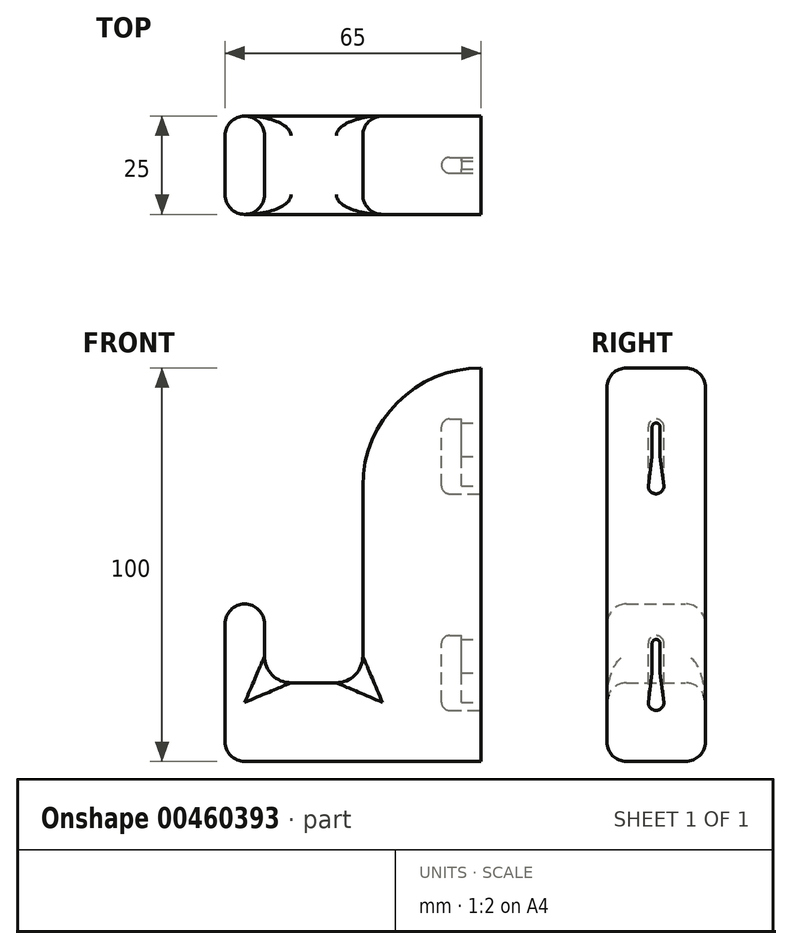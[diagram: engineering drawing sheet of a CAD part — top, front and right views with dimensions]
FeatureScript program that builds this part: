
annotation { "Feature Type Name" : "Feature", "Feature Type Description" : "" }
export const myFeature = defineFeature(function(context is Context, id is Id, definition is map)
    precondition{}
    {
        {
            var Q0;
            Q0=qCreatedBy(makeId("Front.planeOp"),FACE);
            var sketch = newSketch(context, id + "F0", { "sketchPlane" : qUnion([Q0])});
            skLineSegment(sketch, "E0", {"start": v(-32.5, 0) * mm, "end": v(32.5, 0) * mm});
            skLineSegment(sketch, "E1", {"start": v(32.5, 0) * mm, "end": v(32.5, 100) * mm});
            skLineSegment(sketch, "E2", {"start": v(32.5, 100) * mm, "end": v(2.5, 100) * mm});
            skLineSegment(sketch, "E3", {"start": v(2.5, 100) * mm, "end": v(2.5, 20) * mm});
            skLineSegment(sketch, "E4", {"start": v(2.5, 20) * mm, "end": v(-22.5, 20) * mm});
            skLineSegment(sketch, "E5", {"start": v(-22.5, 20) * mm, "end": v(-22.5, 40) * mm});
            skLineSegment(sketch, "E6", {"start": v(-22.5, 40) * mm, "end": v(-32.5, 40) * mm});
            skLineSegment(sketch, "E7", {"start": v(-32.5, 40) * mm, "end": v(-32.5, 0) * mm});
            skSolve(sketch);
        }
        {
            var Q0;
            Q0 = qSketchRegion(id + "F0", true);
            extrude(context, id + "F1", {"entities" : qUnion([Q0]), "endBound" : BoundingType.SYMMETRIC, "depth" : 25 * mm});
        }
        {
            var Q0;
            Q0=makeQuery(id+"F1.opExtrude","SWEPT_EDGE",EDGE,{"disambiguationData":[OSD([sQuery(id+"F0.wireOp",EDGE,"E6"),sQuery(id+"F0.wireOp",EDGE,"E7")])]});
            var Q1;
            Q1=makeQuery(id+"F1.opExtrude","SWEPT_EDGE",EDGE,{"disambiguationData":[OSD([sQuery(id+"F0.wireOp",EDGE,"E0"),sQuery(id+"F0.wireOp",EDGE,"E7")])]});
            var Q2;
            Q2=makeQuery(id+"F1.opExtrude","SWEPT_EDGE",EDGE,{"disambiguationData":[OSD([sQuery(id+"F0.wireOp",EDGE,"E5"),sQuery(id+"F0.wireOp",EDGE,"E6")])]});
            var Q3;
            Q3=makeQuery(id+"F1.opExtrude","CAP_EDGE",EDGE,{"disambiguationData":[OSD([sQuery(id+"F0.wireOp",EDGE,"E4")])],"isStart":false});
            var Q4;
            Q4=makeQuery(id+"F1.opExtrude","CAP_EDGE",EDGE,{"disambiguationData":[OSD([sQuery(id+"F0.wireOp",EDGE,"E4")])],"isStart":true});
            var Q5;
            Q5=makeQuery(id+"F1.opExtrude","CAP_EDGE",EDGE,{"disambiguationData":[OSD([sQuery(id+"F0.wireOp",EDGE,"E7")])],"isStart":false});
            var Q6;
            Q6=makeQuery(id+"F1.opExtrude","CAP_EDGE",EDGE,{"disambiguationData":[OSD([sQuery(id+"F0.wireOp",EDGE,"E5")])],"isStart":false});
            var Q7;
            Q7=makeQuery(id+"F1.opExtrude","CAP_EDGE",EDGE,{"disambiguationData":[OSD([sQuery(id+"F0.wireOp",EDGE,"E6")])],"isStart":false});
            var Q8;
            Q8=makeQuery(id+"F1.opExtrude","CAP_EDGE",EDGE,{"disambiguationData":[OSD([sQuery(id+"F0.wireOp",EDGE,"E6")])],"isStart":true});
            var Q9;
            Q9=makeQuery(id+"F1.opExtrude","CAP_EDGE",EDGE,{"disambiguationData":[OSD([sQuery(id+"F0.wireOp",EDGE,"E7")])],"isStart":true});
            var Q10;
            Q10=makeQuery(id+"F1.opExtrude","CAP_EDGE",EDGE,{"disambiguationData":[OSD([sQuery(id+"F0.wireOp",EDGE,"E5")])],"isStart":true});
            var Q11;
            Q11=makeQuery(id+"F1.opExtrude","CAP_EDGE",EDGE,{"disambiguationData":[OSD([sQuery(id+"F0.wireOp",EDGE,"E0")])],"isStart":false});
            var Q12;
            Q12=makeQuery(id+"F1.opExtrude","CAP_EDGE",EDGE,{"disambiguationData":[OSD([sQuery(id+"F0.wireOp",EDGE,"E0")])],"isStart":true});
            var Q13;
            Q13=makeQuery(id+"F1.opExtrude","CAP_EDGE",EDGE,{"disambiguationData":[OSD([sQuery(id+"F0.wireOp",EDGE,"E3")])],"isStart":false});
            var Q14;
            Q14=makeQuery(id+"F1.opExtrude","CAP_EDGE",EDGE,{"disambiguationData":[OSD([sQuery(id+"F0.wireOp",EDGE,"E3")])],"isStart":true});
            var Q15;
            Q15=makeQuery(id+"F1.opExtrude","CAP_EDGE",EDGE,{"disambiguationData":[OSD([sQuery(id+"F0.wireOp",EDGE,"E2")])],"isStart":false});
            var Q16;
            Q16=makeQuery(id+"F1.opExtrude","CAP_EDGE",EDGE,{"disambiguationData":[OSD([sQuery(id+"F0.wireOp",EDGE,"E2")])],"isStart":true});
            fillet(context, id + "F2", {"entities" : qUnion([Q0, Q1, Q2, Q3, Q4, Q5, Q6, Q7, Q8, Q9, Q10, Q11, Q12, Q13, Q14, Q15, Q16]), "radius" : 5 * mm, "tangentPropagation" : true, "allowEdgeOverflow" : false});
        }
        {
            var Q0;
            Q0=makeQuery(id+"F1.opExtrude","SWEPT_EDGE",EDGE,{"disambiguationData":[OSD([sQuery(id+"F0.wireOp",EDGE,"E2"),sQuery(id+"F0.wireOp",EDGE,"E3")])]});
            fillet(context, id + "F3", {"entities" : qUnion([Q0]), "radius" : 30 * mm, "tangentPropagation" : true, "allowEdgeOverflow" : false});
        }
        {
            var Q0;
            Q0=makeQuery(id+"F1.opExtrude","SWEPT_EDGE",EDGE,{"disambiguationData":[OSD([sQuery(id+"F0.wireOp",EDGE,"E3"),sQuery(id+"F0.wireOp",EDGE,"E4")])]});
            var Q1;
            Q1=makeQuery(id+"F1.opExtrude","SWEPT_EDGE",EDGE,{"disambiguationData":[OSD([sQuery(id+"F0.wireOp",EDGE,"E4"),sQuery(id+"F0.wireOp",EDGE,"E5")])]});
            fillet(context, id + "F4", {"entities" : qUnion([Q0, Q1]), "radius" : 6.75 * mm, "tangentPropagation" : true, "allowEdgeOverflow" : false});
        }
        {
            var Q0;
            Q0=makeQuery(id+"F1.opExtrude","SWEPT_FACE",FACE,{"disambiguationData":[OSD([sQuery(id+"F0.wireOp",EDGE,"E1")])]});
            var sketch = newSketch(context, id + "F5", { "sketchPlane" : qUnion([Q0])});
            skLineSegment(sketch, "E8", {"start": v(0, 15) * mm, "end": v(0, 30) * mm});
            skPoint(sketch, "E8.startSnap0", {"position": v(0, 0) * mm});
            skLineSegment(sketch, "E9", {"start": v(0, 70) * mm, "end": v(0, 85) * mm});
            skArc(sketch, "E10.0.startCap", {"start": v(2, 15) * mm, "mid": v(0, 13) * mm, "end": v(-2, 15) * mm});
            skArc(sketch, "E10.0.endCap", {"start": v(-2, 30) * mm, "mid": v(0, 32) * mm, "end": v(2, 30) * mm});
            skLineSegment(sketch, "E10.0.left", {"start": v(-2, 15) * mm, "end": v(-2, 30) * mm});
            skLineSegment(sketch, "E10.0.right", {"start": v(2, 15) * mm, "end": v(2, 30) * mm});
            skArc(sketch, "E10.1.startCap", {"start": v(2, 70) * mm, "mid": v(0, 68) * mm, "end": v(-2, 70) * mm});
            skArc(sketch, "E10.1.endCap", {"start": v(-2, 85) * mm, "mid": v(0, 87) * mm, "end": v(2, 85) * mm});
            skLineSegment(sketch, "E10.1.left", {"start": v(-2, 70) * mm, "end": v(-2, 85) * mm});
            skLineSegment(sketch, "E10.1.right", {"start": v(2, 70) * mm, "end": v(2, 85) * mm});
            skSolve(sketch);
        }
        {
            var Q0;
            Q0 = qSketchRegion(id + "F5", true);
            extrude(context, id + "F6", {"entities" : qUnion([Q0]), "operationType" : NewBodyOperationType.REMOVE, "oppositeDirection" : true, "depth" : 10 * mm});
        }
        {
            var Q0;
            Q0=makeQuery(id+"F1.opExtrude","SWEPT_FACE",FACE,{"disambiguationData":[OSD([sQuery(id+"F0.wireOp",EDGE,"E1")])]});
            var sketch = newSketch(context, id + "F7", { "sketchPlane" : qUnion([Q0])});
            skArc(sketch, "E11", {"start": v(1, 30) * mm, "mid": v(0, 31) * mm, "end": v(-1, 30) * mm});
            skLineSegment(sketch, "E12", {"start": v(2, 15) * mm, "end": v(2, 30) * mm});
            skArc(sketch, "E13", {"start": v(2, 30) * mm, "mid": v(0, 32) * mm, "end": v(-2, 30) * mm});
            skLineSegment(sketch, "E14", {"start": v(-2, 30) * mm, "end": v(-2, 15) * mm});
            skLineSegment(sketch, "E15", {"start": v(-2, 15) * mm, "end": v(-1, 22.5) * mm});
            skLineSegment(sketch, "E16", {"start": v(-1, 22.5) * mm, "end": v(-1, 30) * mm});
            skLineSegment(sketch, "E17", {"start": v(1, 30) * mm, "end": v(1, 22.5) * mm});
            skLineSegment(sketch, "E18", {"start": v(1, 22.5) * mm, "end": v(2, 15) * mm});
            skLineSegment(sketch, "E19.0.1.0", {"start": v(1, 77.5) * mm, "end": v(2, 70) * mm});
            skLineSegment(sketch, "E19.0.1.1", {"start": v(-1, 77.5) * mm, "end": v(-1, 85) * mm});
            skLineSegment(sketch, "E19.0.1.2", {"start": v(-2, 70) * mm, "end": v(-1, 77.5) * mm});
            skLineSegment(sketch, "E19.0.1.3", {"start": v(1, 85) * mm, "end": v(1, 77.5) * mm});
            skArc(sketch, "E19.0.1.4", {"start": v(1, 85) * mm, "mid": v(0, 86) * mm, "end": v(-1, 85) * mm});
            skLineSegment(sketch, "E19.0.1.5", {"start": v(2, 70) * mm, "end": v(2, 85) * mm});
            skLineSegment(sketch, "E19.0.1.6", {"start": v(-2, 85) * mm, "end": v(-2, 70) * mm});
            skArc(sketch, "E19.0.1.7", {"start": v(2, 85) * mm, "mid": v(0, 87) * mm, "end": v(-2, 85) * mm});
            skLineSegment(sketch, "E19.direction1", {"start": v(-2, 15) * mm, "end": v(23, 15) * mm, "construction": true});
            skLineSegment(sketch, "E19.direction2", {"start": v(-2, 15) * mm, "end": v(-2, 70) * mm, "construction": true});
            skSolve(sketch);
        }
        {
            var Q0;
            Q0 = qSketchRegion(id + "F7", true);
            extrude(context, id + "F8", {"entities" : qUnion([Q0]), "operationType" : NewBodyOperationType.ADD, "oppositeDirection" : true, "depth" : 5 * mm});
        }
        {
            var Q0;
            Q0=makeQuery(id+"F6.boolean.opBoolean","COPY",FACE,{"derivedFrom":makeQuery(id+"F6.opExtrude","CAP_FACE",FACE,{"disambiguationData":[OSD([sQuery(id+"F5.wireOp",EDGE,"E10.0.startCap"),sQuery(id+"F5.wireOp",EDGE,"E10.0.endCap"),sQuery(id+"F5.wireOp",EDGE,"E10.0.left"),sQuery(id+"F5.wireOp",EDGE,"E10.0.right")])],"isStart":false})});
            var Q1;
            Q1=makeQuery(id+"F6.boolean.opBoolean","COPY",FACE,{"derivedFrom":makeQuery(id+"F6.opExtrude","CAP_FACE",FACE,{"disambiguationData":[OSD([sQuery(id+"F5.wireOp",EDGE,"E10.1.startCap"),sQuery(id+"F5.wireOp",EDGE,"E10.1.endCap"),sQuery(id+"F5.wireOp",EDGE,"E10.1.left"),sQuery(id+"F5.wireOp",EDGE,"E10.1.right")])],"isStart":false})});
            fillet(context, id + "F9", {"entities" : qUnion([Q0, Q1]), "radius" : 2 * mm, "tangentPropagation" : true, "allowEdgeOverflow" : false});
        }
    });
